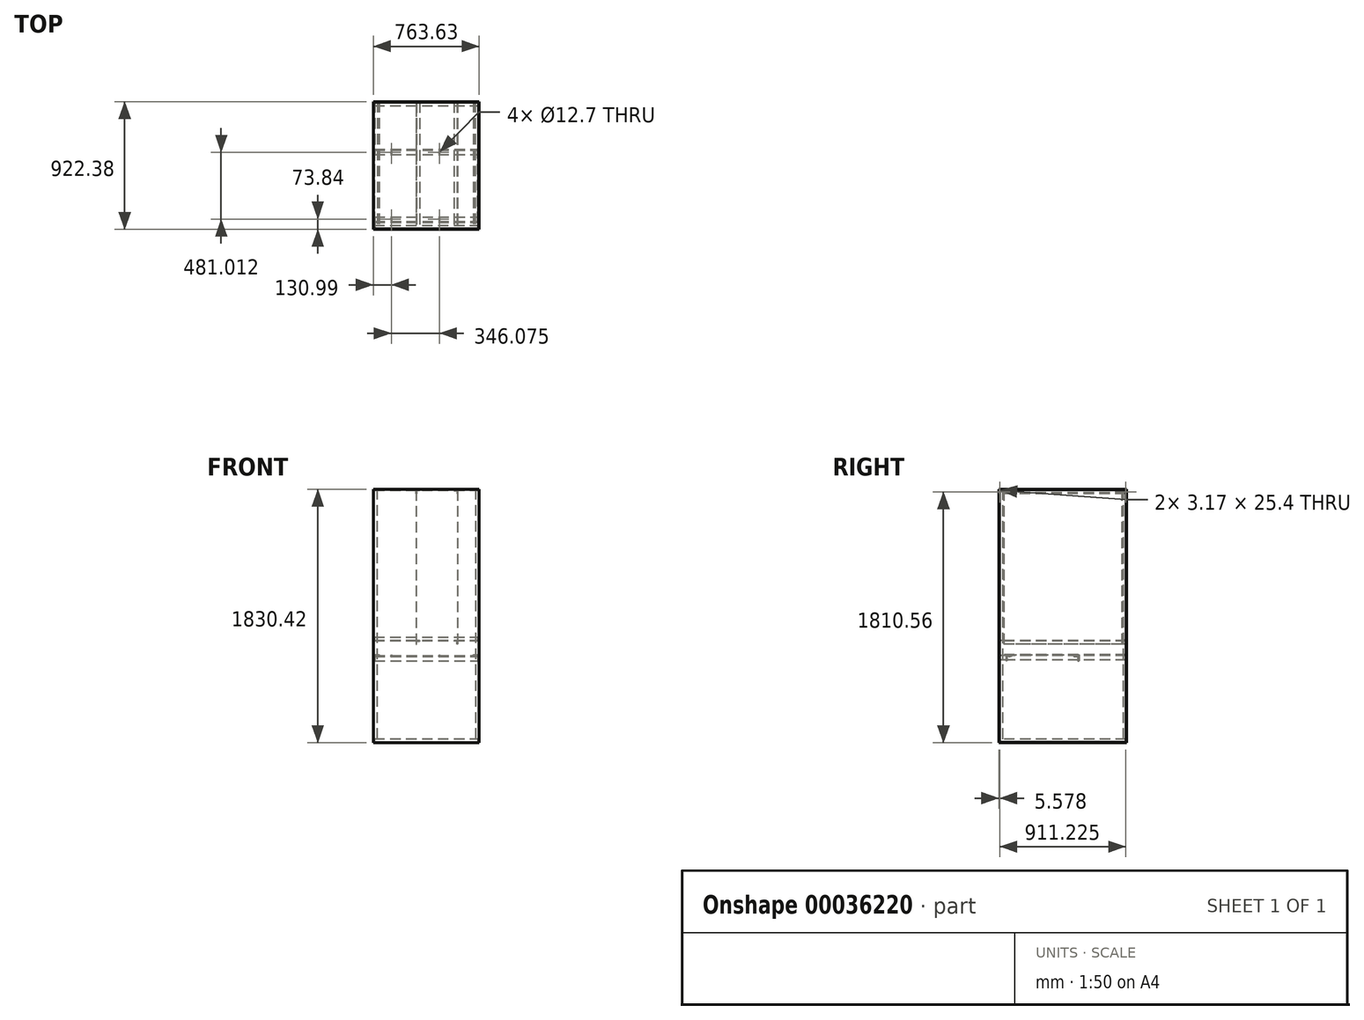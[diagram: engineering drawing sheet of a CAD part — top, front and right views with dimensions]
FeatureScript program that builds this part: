
annotation { "Feature Type Name" : "Feature", "Feature Type Description" : "" }
export const myFeature = defineFeature(function(context is Context, id is Id, definition is map)
    precondition{}
    {
        {
            var Q0;
            Q0=qCreatedBy(makeId("Front.planeOp"),FACE);
            var sketch = newSketch(context, id + "F0", { "sketchPlane" : qUnion([Q0])});
            skLineSegment(sketch, "E0", {"start": v(0, 0) * mm, "end": v(0, 25.4) * mm});
            skLineSegment(sketch, "E1", {"start": v(0, 25.4) * mm, "end": v(3.18, 25.4) * mm});
            skLineSegment(sketch, "E2", {"start": v(3.18, 25.4) * mm, "end": v(3.18, 3.17) * mm});
            skLineSegment(sketch, "E3", {"start": v(3.18, 3.17) * mm, "end": v(25.4, 3.17) * mm});
            skLineSegment(sketch, "E4", {"start": v(25.4, 3.17) * mm, "end": v(25.4, 0) * mm});
            skLineSegment(sketch, "E5", {"start": v(25.4, 0) * mm, "end": v(0, 0) * mm});
            skLineSegment(sketch, "E6", {"start": v(730.25, 0) * mm, "end": v(755.65, 0) * mm});
            skLineSegment(sketch, "E7", {"start": v(755.65, 0) * mm, "end": v(755.65, 25.4) * mm});
            skLineSegment(sketch, "E8", {"start": v(755.65, 25.4) * mm, "end": v(752.48, 25.4) * mm});
            skLineSegment(sketch, "E9", {"start": v(752.47, 25.4) * mm, "end": v(752.47, 3.18) * mm});
            skLineSegment(sketch, "E10", {"start": v(752.47, 3.18) * mm, "end": v(730.25, 3.18) * mm});
            skLineSegment(sketch, "E11", {"start": v(730.25, 3.18) * mm, "end": v(730.25, 0) * mm});
            skLineSegment(sketch, "E12", {"start": v(730.25, 1828.8) * mm, "end": v(755.65, 1828.8) * mm});
            skLineSegment(sketch, "E13", {"start": v(755.65, 1828.8) * mm, "end": v(755.65, 1803.4) * mm});
            skLineSegment(sketch, "E14", {"start": v(755.65, 1803.4) * mm, "end": v(752.48, 1803.4) * mm});
            skLineSegment(sketch, "E15", {"start": v(752.48, 1803.4) * mm, "end": v(752.48, 1825.62) * mm});
            skLineSegment(sketch, "E16", {"start": v(752.47, 1825.62) * mm, "end": v(730.25, 1825.62) * mm});
            skLineSegment(sketch, "E17", {"start": v(730.25, 1825.62) * mm, "end": v(730.25, 1828.8) * mm});
            skLineSegment(sketch, "E18", {"start": v(0, 1803.4) * mm, "end": v(0, 1828.8) * mm});
            skLineSegment(sketch, "E19", {"start": v(0, 1828.8) * mm, "end": v(25.4, 1828.8) * mm});
            skLineSegment(sketch, "E20", {"start": v(25.4, 1828.8) * mm, "end": v(25.4, 1825.62) * mm});
            skLineSegment(sketch, "E21", {"start": v(25.4, 1825.62) * mm, "end": v(3.17, 1825.62) * mm});
            skLineSegment(sketch, "E22", {"start": v(3.17, 1825.62) * mm, "end": v(3.17, 1803.4) * mm});
            skLineSegment(sketch, "E23", {"start": v(3.17, 1803.4) * mm, "end": v(0, 1803.4) * mm});
            skLineSegment(sketch, "E24", {"start": v(717.55, 635) * mm, "end": v(755.65, 635) * mm});
            skLineSegment(sketch, "E25", {"start": v(755.65, 635) * mm, "end": v(755.65, 596.9) * mm});
            skLineSegment(sketch, "E26", {"start": v(755.65, 596.9) * mm, "end": v(749.3, 596.9) * mm});
            skLineSegment(sketch, "E27", {"start": v(749.3, 596.9) * mm, "end": v(749.3, 628.65) * mm});
            skLineSegment(sketch, "E28", {"start": v(749.3, 628.65) * mm, "end": v(717.55, 628.65) * mm});
            skLineSegment(sketch, "E29", {"start": v(717.55, 628.65) * mm, "end": v(717.55, 635) * mm});
            skLineSegment(sketch, "E30", {"start": v(0, 596.9) * mm, "end": v(0, 635) * mm});
            skLineSegment(sketch, "E31", {"start": v(0, 635) * mm, "end": v(38.1, 635) * mm});
            skLineSegment(sketch, "E32", {"start": v(38.1, 635) * mm, "end": v(38.1, 628.65) * mm});
            skLineSegment(sketch, "E33", {"start": v(38.1, 628.65) * mm, "end": v(6.35, 628.65) * mm});
            skLineSegment(sketch, "E34", {"start": v(6.35, 628.65) * mm, "end": v(6.35, 596.9) * mm});
            skLineSegment(sketch, "E35", {"start": v(6.35, 596.9) * mm, "end": v(0, 596.9) * mm});
            skLineSegment(sketch, "E36", {"start": v(577.85, 736.6) * mm, "end": v(603.25, 736.6) * mm});
            skLineSegment(sketch, "E37", {"start": v(603.25, 736.6) * mm, "end": v(603.25, 711.2) * mm});
            skLineSegment(sketch, "E38", {"start": v(603.25, 711.2) * mm, "end": v(600.07, 711.2) * mm});
            skLineSegment(sketch, "E39", {"start": v(600.07, 711.2) * mm, "end": v(600.07, 733.43) * mm});
            skLineSegment(sketch, "E40", {"start": v(600.07, 733.43) * mm, "end": v(577.85, 733.43) * mm});
            skLineSegment(sketch, "E41", {"start": v(577.85, 1822.45) * mm, "end": v(603.25, 1822.45) * mm});
            skLineSegment(sketch, "E42", {"start": v(603.25, 1822.45) * mm, "end": v(603.25, 1797.05) * mm});
            skLineSegment(sketch, "E43", {"start": v(603.25, 1797.05) * mm, "end": v(600.07, 1797.05) * mm});
            skLineSegment(sketch, "E44", {"start": v(600.07, 1797.05) * mm, "end": v(600.07, 1819.27) * mm});
            skLineSegment(sketch, "E45", {"start": v(600.07, 1819.27) * mm, "end": v(577.85, 1819.27) * mm});
            skLineSegment(sketch, "E46", {"start": v(577.85, 1819.27) * mm, "end": v(577.85, 1822.45) * mm});
            skLineSegment(sketch, "E47", {"start": v(577.85, 736.6) * mm, "end": v(577.85, 733.43) * mm});
            skLineSegment(sketch, "E48", {"start": v(600.07, 733.43) * mm, "end": v(600.07, 736.6) * mm, "construction": true});
            skLineSegment(sketch, "E49", {"start": v(600.07, 1819.27) * mm, "end": v(600.07, 1822.45) * mm, "construction": true});
            skLineSegment(sketch, "E50.MirrorCS", {"start": v(307.97, 733.43) * mm, "end": v(307.97, 736.6) * mm, "construction": true});
            skLineSegment(sketch, "E51.MirrorCS", {"start": v(330.2, 736.6) * mm, "end": v(330.2, 733.43) * mm});
            skLineSegment(sketch, "E52.MirrorCS", {"start": v(330.2, 736.6) * mm, "end": v(304.8, 736.6) * mm});
            skLineSegment(sketch, "E53.MirrorCS", {"start": v(307.97, 733.43) * mm, "end": v(330.2, 733.43) * mm});
            skLineSegment(sketch, "E54.MirrorCS", {"start": v(304.8, 736.6) * mm, "end": v(304.8, 711.2) * mm});
            skLineSegment(sketch, "E55.MirrorCS", {"start": v(307.97, 711.2) * mm, "end": v(307.97, 733.43) * mm});
            skLineSegment(sketch, "E56.MirrorCS", {"start": v(304.8, 711.2) * mm, "end": v(307.97, 711.2) * mm});
            skLineSegment(sketch, "E57.MirrorCS", {"start": v(307.97, 1819.27) * mm, "end": v(307.97, 1822.45) * mm, "construction": true});
            skLineSegment(sketch, "E58.MirrorCS", {"start": v(330.2, 1822.45) * mm, "end": v(304.8, 1822.45) * mm});
            skLineSegment(sketch, "E59.MirrorCS", {"start": v(307.97, 1819.27) * mm, "end": v(330.2, 1819.27) * mm});
            skLineSegment(sketch, "E60.MirrorCS", {"start": v(304.8, 1822.45) * mm, "end": v(304.8, 1797.05) * mm});
            skLineSegment(sketch, "E61.MirrorCS", {"start": v(307.97, 1797.05) * mm, "end": v(307.97, 1819.27) * mm});
            skLineSegment(sketch, "E62.MirrorCS", {"start": v(330.2, 1819.27) * mm, "end": v(330.2, 1822.45) * mm});
            skLineSegment(sketch, "E63.MirrorCS", {"start": v(304.8, 1797.05) * mm, "end": v(307.97, 1797.05) * mm});
            skSolve(sketch);
        }
        {
            var Q0;
            Q0=qSketchRegion(id+"F0",true);
            extrude(context, id + "F1", {"entities" : qUnion([Q0]), "oppositeDirection" : true, "depth" : 914.4 * mm});
        }
        {
            var Q0;
            Q0=qCreatedBy(makeId("Top.planeOp"),FACE);
            var sketch = newSketch(context, id + "F2", { "sketchPlane" : qUnion([Q0])});
            skLineSegment(sketch, "E64", {"start": v(-3.18, 22.23) * mm, "end": v(-3.18, -3.18) * mm});
            skLineSegment(sketch, "E65", {"start": v(-3.18, -3.18) * mm, "end": v(22.23, -3.18) * mm});
            skLineSegment(sketch, "E66", {"start": v(22.23, -3.18) * mm, "end": v(22.23, 0) * mm});
            skLineSegment(sketch, "E67", {"start": v(22.23, 0) * mm, "end": v(0, 0) * mm});
            skLineSegment(sketch, "E68", {"start": v(0, 0) * mm, "end": v(0, 22.23) * mm});
            skLineSegment(sketch, "E69", {"start": v(0, 22.23) * mm, "end": v(-3.18, 22.23) * mm});
            skLineSegment(sketch, "E70", {"start": v(733.42, -3.18) * mm, "end": v(758.83, -3.18) * mm});
            skLineSegment(sketch, "E71", {"start": v(758.83, -3.18) * mm, "end": v(758.83, 22.23) * mm});
            skLineSegment(sketch, "E72", {"start": v(758.83, 22.23) * mm, "end": v(755.65, 22.23) * mm});
            skLineSegment(sketch, "E73", {"start": v(755.65, 22.23) * mm, "end": v(755.65, 0) * mm});
            skLineSegment(sketch, "E74", {"start": v(755.65, 0) * mm, "end": v(733.42, 0) * mm});
            skLineSegment(sketch, "E75", {"start": v(733.42, 0) * mm, "end": v(733.42, -3.18) * mm});
            skLineSegment(sketch, "E76", {"start": v(0, 892.17) * mm, "end": v(0, 914.4) * mm});
            skLineSegment(sketch, "E77", {"start": v(0, 914.4) * mm, "end": v(22.23, 914.4) * mm});
            skLineSegment(sketch, "E78", {"start": v(22.23, 914.4) * mm, "end": v(22.23, 917.58) * mm});
            skLineSegment(sketch, "E79", {"start": v(22.23, 917.58) * mm, "end": v(-3.18, 917.58) * mm});
            skLineSegment(sketch, "E80", {"start": v(-3.18, 917.58) * mm, "end": v(-3.18, 892.17) * mm});
            skLineSegment(sketch, "E81", {"start": v(-3.18, 892.17) * mm, "end": v(0, 892.17) * mm});
            skLineSegment(sketch, "E82", {"start": v(733.42, 914.4) * mm, "end": v(755.65, 914.4) * mm});
            skLineSegment(sketch, "E83", {"start": v(755.65, 914.4) * mm, "end": v(755.65, 892.17) * mm});
            skLineSegment(sketch, "E84", {"start": v(755.65, 892.18) * mm, "end": v(758.83, 892.18) * mm});
            skLineSegment(sketch, "E85", {"start": v(758.83, 892.17) * mm, "end": v(758.83, 917.58) * mm});
            skLineSegment(sketch, "E86", {"start": v(758.83, 917.58) * mm, "end": v(733.42, 917.58) * mm});
            skLineSegment(sketch, "E87", {"start": v(733.42, 917.58) * mm, "end": v(733.42, 914.4) * mm});
            skSolve(sketch);
        }
        {
            var Q0;
            Q0=qSketchRegion(id+"F2",true);
            extrude(context, id + "F3", {"entities" : qUnion([Q0]), "depth" : 1828.8 * mm});
        }
        {
            var Q0;
            Q0=makeQuery(id+"F1.opExtrude","SWEPT_FACE",FACE,{"disambiguationData":[OSD([sQuery(id+"F0.wireOp",EDGE,"E15")])]});
            var sketch = newSketch(context, id + "F4", { "sketchPlane" : qUnion([Q0])});
            skLineSegment(sketch, "E88", {"start": v(-25.4, 3.18) * mm, "end": v(0, 3.18) * mm});
            skLineSegment(sketch, "E89", {"start": v(0, 3.18) * mm, "end": v(0, 28.58) * mm});
            skLineSegment(sketch, "E90", {"start": v(0, 28.58) * mm, "end": v(-3.17, 28.58) * mm});
            skLineSegment(sketch, "E91", {"start": v(-3.18, 28.58) * mm, "end": v(-3.17, 6.35) * mm});
            skLineSegment(sketch, "E92", {"start": v(-3.18, 6.35) * mm, "end": v(-25.4, 6.35) * mm});
            skLineSegment(sketch, "E93", {"start": v(-25.4, 6.35) * mm, "end": v(-25.4, 3.18) * mm});
            skLineSegment(sketch, "E94", {"start": v(0, 1800.22) * mm, "end": v(0, 1825.62) * mm});
            skLineSegment(sketch, "E95", {"start": v(0, 1825.62) * mm, "end": v(-25.4, 1825.62) * mm});
            skLineSegment(sketch, "E96", {"start": v(-25.4, 1825.62) * mm, "end": v(-25.4, 1822.45) * mm});
            skLineSegment(sketch, "E97", {"start": v(-25.4, 1822.45) * mm, "end": v(-3.18, 1822.45) * mm});
            skLineSegment(sketch, "E98", {"start": v(-3.18, 1822.45) * mm, "end": v(-3.18, 1800.22) * mm});
            skLineSegment(sketch, "E99", {"start": v(-3.18, 1800.22) * mm, "end": v(0, 1800.22) * mm});
            skLineSegment(sketch, "E100", {"start": v(-914.4, 1800.22) * mm, "end": v(-914.4, 1825.62) * mm});
            skLineSegment(sketch, "E101", {"start": v(-914.4, 1825.62) * mm, "end": v(-889, 1825.62) * mm});
            skLineSegment(sketch, "E102", {"start": v(-889, 1825.62) * mm, "end": v(-889, 1822.45) * mm});
            skLineSegment(sketch, "E103", {"start": v(-889, 1822.45) * mm, "end": v(-911.22, 1822.45) * mm});
            skLineSegment(sketch, "E104", {"start": v(-911.23, 1822.45) * mm, "end": v(-911.23, 1800.22) * mm});
            skLineSegment(sketch, "E105", {"start": v(-911.22, 1800.22) * mm, "end": v(-914.4, 1800.22) * mm});
            skLineSegment(sketch, "E106", {"start": v(-914.4, 28.58) * mm, "end": v(-914.4, 3.18) * mm});
            skLineSegment(sketch, "E107", {"start": v(-914.4, 3.18) * mm, "end": v(-889, 3.18) * mm});
            skLineSegment(sketch, "E108", {"start": v(-889, 3.18) * mm, "end": v(-889, 6.35) * mm});
            skLineSegment(sketch, "E109", {"start": v(-889, 6.35) * mm, "end": v(-911.22, 6.35) * mm});
            skLineSegment(sketch, "E110", {"start": v(-911.22, 6.35) * mm, "end": v(-911.22, 28.58) * mm});
            skLineSegment(sketch, "E111", {"start": v(-911.22, 28.58) * mm, "end": v(-914.4, 28.58) * mm});
            skLineSegment(sketch, "E112", {"start": v(-573.09, 590.55) * mm, "end": v(-573.09, 628.65) * mm});
            skLineSegment(sketch, "E113", {"start": v(-573.09, 628.65) * mm, "end": v(-534.99, 628.65) * mm});
            skLineSegment(sketch, "E114", {"start": v(-534.99, 628.65) * mm, "end": v(-534.99, 622.3) * mm});
            skLineSegment(sketch, "E115", {"start": v(-534.99, 622.3) * mm, "end": v(-566.74, 622.3) * mm});
            skLineSegment(sketch, "E116", {"start": v(-566.74, 622.3) * mm, "end": v(-566.74, 590.55) * mm});
            skLineSegment(sketch, "E117", {"start": v(-566.74, 590.55) * mm, "end": v(-573.09, 590.55) * mm});
            skLineSegment(sketch, "E118", {"start": v(-550.86, 622.3) * mm, "end": v(-550.86, 628.65) * mm, "construction": true});
            skLineSegment(sketch, "E119", {"start": v(-47.63, 590.55) * mm, "end": v(-47.63, 628.65) * mm});
            skLineSegment(sketch, "E120", {"start": v(-47.63, 628.65) * mm, "end": v(-85.72, 628.65) * mm});
            skLineSegment(sketch, "E121", {"start": v(-85.73, 628.65) * mm, "end": v(-85.73, 622.3) * mm});
            skLineSegment(sketch, "E122", {"start": v(-85.72, 622.3) * mm, "end": v(-53.98, 622.3) * mm});
            skLineSegment(sketch, "E123", {"start": v(-53.98, 622.3) * mm, "end": v(-53.98, 590.55) * mm});
            skLineSegment(sketch, "E124", {"start": v(-53.97, 590.55) * mm, "end": v(-47.63, 590.55) * mm});
            skLineSegment(sketch, "E125", {"start": v(-69.85, 622.3) * mm, "end": v(-69.85, 628.65) * mm, "construction": true});
            skLineSegment(sketch, "E126", {"start": v(-550.86, 625.48) * mm, "end": v(-69.85, 625.48) * mm, "construction": true});
            skLineSegment(sketch, "E127", {"start": v(0, 736.6) * mm, "end": v(0, 762) * mm});
            skLineSegment(sketch, "E128", {"start": v(0, 762) * mm, "end": v(-3.17, 762) * mm});
            skLineSegment(sketch, "E129", {"start": v(-3.17, 762) * mm, "end": v(-3.17, 739.78) * mm});
            skLineSegment(sketch, "E130", {"start": v(-3.17, 739.78) * mm, "end": v(-25.4, 739.78) * mm});
            skLineSegment(sketch, "E131", {"start": v(-25.4, 739.78) * mm, "end": v(-25.4, 736.6) * mm});
            skLineSegment(sketch, "E132", {"start": v(-25.4, 736.6) * mm, "end": v(0, 736.6) * mm});
            skLineSegment(sketch, "E133", {"start": v(-889, 736.6) * mm, "end": v(-914.4, 736.6) * mm});
            skLineSegment(sketch, "E134", {"start": v(-914.4, 736.6) * mm, "end": v(-914.4, 762) * mm});
            skLineSegment(sketch, "E135", {"start": v(-914.4, 762) * mm, "end": v(-911.22, 762) * mm});
            skLineSegment(sketch, "E136", {"start": v(-911.23, 762) * mm, "end": v(-911.23, 739.78) * mm});
            skLineSegment(sketch, "E137", {"start": v(-911.22, 739.78) * mm, "end": v(-889, 739.78) * mm});
            skLineSegment(sketch, "E138", {"start": v(-889, 739.78) * mm, "end": v(-889, 736.6) * mm});
            skSolve(sketch);
        }
        {
            var Q0;
            Q0=qSketchRegion(id+"F4",true);
            var Q1;
            Q1=makeQuery(id+"F1.opExtrude","SWEPT_FACE",FACE,{"disambiguationData":[OSD([sQuery(id+"F0.wireOp",EDGE,"E2")])]});
            extrude(context, id + "F5", {"entities" : qUnion([Q0]), "endBound" : BoundingType.UP_TO_SURFACE, "endBoundEntityFace" : qUnion([Q1]), "depth" : 25.4 * mm});
        }
        {
            var Q0;
            Q0=makeQuery(id+"F5.opExtrude","SWEPT_FACE",FACE,{"disambiguationData":[OSD([sQuery(id+"F4.wireOp",EDGE,"E115")])]});
            var sketch = newSketch(context, id + "F6", { "sketchPlane" : qUnion([Q0])});
            skLineSegment(sketch, "E139.bottom", {"start": v(127, -69.85) * mm, "end": v(473.07, -69.85) * mm, "construction": true});
            skLineSegment(sketch, "E139.top", {"start": v(127, -550.86) * mm, "end": v(473.07, -550.86) * mm, "construction": true});
            skLineSegment(sketch, "E139.left", {"start": v(473.07, -69.85) * mm, "end": v(473.07, -550.86) * mm, "construction": true});
            skLineSegment(sketch, "E139.right", {"start": v(127, -69.85) * mm, "end": v(127, -550.86) * mm, "construction": true});
            skLineSegment(sketch, "E140", {"start": v(473.07, -550.86) * mm, "end": v(3.17, -550.86) * mm, "construction": true});
            skLineSegment(sketch, "E141", {"start": v(127, -550.86) * mm, "end": v(752.47, -550.86) * mm, "construction": true});
            skCircle(sketch, "E142", {"center": v(127, -69.85) * mm, "radius": 6.35 * mm});
            skCircle(sketch, "E143", {"center": v(473.07, -69.85) * mm, "radius": 6.35 * mm});
            skCircle(sketch, "E144", {"center": v(473.07, -550.86) * mm, "radius": 6.35 * mm});
            skCircle(sketch, "E145", {"center": v(127, -550.86) * mm, "radius": 6.35 * mm});
            skLineSegment(sketch, "E146.bottom", {"start": v(3.17, -47.62) * mm, "end": v(6.35, -47.62) * mm});
            skLineSegment(sketch, "E146.top", {"start": v(3.17, -573.09) * mm, "end": v(6.35, -573.09) * mm});
            skLineSegment(sketch, "E146.left", {"start": v(3.17, -47.62) * mm, "end": v(3.17, -573.09) * mm});
            skLineSegment(sketch, "E146.right", {"start": v(6.35, -47.62) * mm, "end": v(6.35, -573.09) * mm});
            skLineSegment(sketch, "E147.bottom", {"start": v(749.3, -47.62) * mm, "end": v(752.47, -47.62) * mm});
            skLineSegment(sketch, "E147.top", {"start": v(749.3, -573.09) * mm, "end": v(752.47, -573.09) * mm});
            skLineSegment(sketch, "E147.left", {"start": v(749.3, -47.62) * mm, "end": v(749.3, -573.09) * mm});
            skLineSegment(sketch, "E147.right", {"start": v(752.47, -47.62) * mm, "end": v(752.47, -573.09) * mm});
            skSolve(sketch);
        }
        {
            var Q0;
            Q0=makeQuery(id+"F6.imprint","IMPRINT",FACE,{"disambiguationData":[TD([[makeQuery(id+"F6.imprint","IMPRINT",EDGE,{"derivedFrom":sQuery(id+"F6.wireOp",EDGE,"E143")}),1.0]])]});
            var Q1;
            Q1=makeQuery(id+"F6.imprint","IMPRINT",FACE,{"disambiguationData":[TD([[makeQuery(id+"F6.imprint","IMPRINT",EDGE,{"derivedFrom":sQuery(id+"F6.wireOp",EDGE,"E144")}),1.0]])]});
            var Q2;
            Q2=makeQuery(id+"F6.imprint","IMPRINT",FACE,{"disambiguationData":[TD([[makeQuery(id+"F6.imprint","IMPRINT",EDGE,{"derivedFrom":sQuery(id+"F6.wireOp",EDGE,"E145")}),1.0]])]});
            var Q3;
            Q3=makeQuery(id+"F6.imprint","IMPRINT",FACE,{"disambiguationData":[TD([[makeQuery(id+"F6.imprint","IMPRINT",EDGE,{"derivedFrom":sQuery(id+"F6.wireOp",EDGE,"E142")}),1.0]])]});
            var Q4;
            {var subQ5=sQuery(id+"F6.wireOp",EDGE,"E146.bottom");Q4=makeQuery(id+"F6.imprint","IMPRINT",FACE,{"disambiguationData":[TD([[makeQuery(id+"F6.imprint","IMPRINT",EDGE,{"derivedFrom":subQ5}),-1.0]])]});}
            var Q5;
            {var subQ5=sQuery(id+"F6.wireOp",EDGE,"E147.bottom");Q5=makeQuery(id+"F6.imprint","IMPRINT",FACE,{"disambiguationData":[TD([[makeQuery(id+"F6.imprint","IMPRINT",EDGE,{"derivedFrom":subQ5}),-1.0]])]});}
            var Q6;
            {var subQ5=sQuery(id+"F6.wireOp",EDGE,"E146.top");Q6=makeQuery(id+"F6.imprint","IMPRINT",FACE,{"disambiguationData":[TD([[makeQuery(id+"F6.imprint","IMPRINT",EDGE,{"derivedFrom":subQ5}),1.0]])]});}
            var Q7;
            {var subQ0=sQuery(id+"F4.wireOp",EDGE,"E115");var subQ4=sQuery(id+"F6.wireOp",EDGE,"E146.left");var subQ6=makeQuery(id+"F5.opExtrude","SWEPT_EDGE",EDGE,{"disambiguationData":[OSD([sQuery(id+"F4.wireOp",EDGE,"E114"),subQ0])]});var subQ8=makeQuery(id+"F6.imprint","INTERSECT",VERTEX,{"derivedFrom":[subQ6,subQ4]});Q7=makeQuery(id+"F6.imprint","IMPRINT",FACE,{"disambiguationData":[TD([[makeQuery(id+"F6.imprint","IMPRINT",EDGE,{"disambiguationData":[TD([[subQ8,-1.0]])],"derivedFrom":subQ4}),1.0]])]});}
            var Q8;
            {var subQ0=sQuery(id+"F4.wireOp",EDGE,"E115");var subQ2=sQuery(id+"F6.wireOp",EDGE,"E147.left");var subQ6=makeQuery(id+"F5.opExtrude","SWEPT_EDGE",EDGE,{"disambiguationData":[OSD([sQuery(id+"F4.wireOp",EDGE,"E114"),subQ0])]});var subQ7=makeQuery(id+"F6.imprint","INTERSECT",VERTEX,{"derivedFrom":[subQ6,subQ2]});Q8=makeQuery(id+"F6.imprint","IMPRINT",FACE,{"disambiguationData":[TD([[makeQuery(id+"F6.imprint","IMPRINT",EDGE,{"disambiguationData":[TD([[subQ7,-1.0]])],"derivedFrom":subQ2}),1.0]])]});}
            var Q9;
            {var subQ5=sQuery(id+"F6.wireOp",EDGE,"E147.top");Q9=makeQuery(id+"F6.imprint","IMPRINT",FACE,{"disambiguationData":[TD([[makeQuery(id+"F6.imprint","IMPRINT",EDGE,{"derivedFrom":subQ5}),1.0]])]});}
            var Q10;
            Q10=makeQuery(id+"F5.opExtrude","SWEPT_FACE",FACE,{"disambiguationData":[OSD([sQuery(id+"F4.wireOp",EDGE,"E117")])]});
            extrude(context, id + "F7", {"entities" : qUnion([Q0, Q1, Q2, Q3, Q4, Q5, Q6, Q7, Q8, Q9]), "operationType" : NewBodyOperationType.REMOVE, "oppositeDirection" : true, "endBoundEntityFace" : qUnion([Q10]), "depth" : 50.8 * mm, "hasSecondDirection" : true, "secondDirectionOppositeDirection" : false, "secondDirectionDepth" : 50.8 * mm});
        }
        {
            var Q0;
            Q0=makeQuery(id+"F1.opExtrude","SWEPT_FACE",FACE,{"disambiguationData":[OSD([sQuery(id+"F0.wireOp",EDGE,"E37")])]});
            var sketch = newSketch(context, id + "F8", { "sketchPlane" : qUnion([Q0])});
            skLineSegment(sketch, "E148.bottom", {"start": v(31.75, 1822.45) * mm, "end": v(882.65, 1822.45) * mm});
            skLineSegment(sketch, "E148.top", {"start": v(31.75, 711.2) * mm, "end": v(882.65, 711.2) * mm});
            skLineSegment(sketch, "E148.left", {"start": v(31.75, 1822.45) * mm, "end": v(31.75, 711.2) * mm});
            skLineSegment(sketch, "E148.right", {"start": v(882.65, 1822.45) * mm, "end": v(882.65, 711.2) * mm});
            skSolve(sketch);
        }
        {
            var Q0;
            Q0=qSketchRegion(id+"F8",true);
            extrude(context, id + "F9", {"entities" : qUnion([Q0]), "depth" : 1.02 * mm});
        }
        {
            var Q0;
            Q0=makeQuery(id+"F1.opExtrude","SWEPT_FACE",FACE,{"disambiguationData":[OSD([sQuery(id+"F0.wireOp",EDGE,"E46")])]});
            var sketch = newSketch(context, id + "F10", { "sketchPlane" : qUnion([Q0])});
            skLineSegment(sketch, "E149.bottom", {"start": v(-3.18, 1822.45) * mm, "end": v(0, 1822.45) * mm});
            skLineSegment(sketch, "E149.top", {"start": v(-3.18, 1797.05) * mm, "end": v(0, 1797.05) * mm});
            skLineSegment(sketch, "E149.left", {"start": v(-3.18, 1822.45) * mm, "end": v(-3.18, 1797.05) * mm});
            skLineSegment(sketch, "E149.right", {"start": v(0, 1822.45) * mm, "end": v(0, 1797.05) * mm});
            skLineSegment(sketch, "E150.bottom", {"start": v(-914.4, 1822.45) * mm, "end": v(-911.22, 1822.45) * mm});
            skLineSegment(sketch, "E150.top", {"start": v(-914.4, 1797.05) * mm, "end": v(-911.22, 1797.05) * mm});
            skLineSegment(sketch, "E150.left", {"start": v(-914.4, 1822.45) * mm, "end": v(-914.4, 1797.05) * mm});
            skLineSegment(sketch, "E150.right", {"start": v(-911.22, 1822.45) * mm, "end": v(-911.22, 1797.05) * mm});
            skSolve(sketch);
        }
        {
            var Q0;
            Q0=qSketchRegion(id+"F10",true);
            var Q1;
            Q1=makeQuery(id+"F1.opExtrude","SWEPT_FACE",FACE,{"disambiguationData":[OSD([sQuery(id+"F0.wireOp",EDGE,"E60.MirrorCS")])]});
            extrude(context, id + "F11", {"entities" : qUnion([Q0]), "operationType" : NewBodyOperationType.REMOVE, "endBound" : BoundingType.THROUGH_ALL, "depth" : 25.4 * mm, "hasSecondDirection" : true, "secondDirectionBound" : BoundingType.THROUGH_ALL, "secondDirectionOppositeDirection" : true, "secondDirectionBoundEntityFace" : qUnion([Q1]), "secondDirectionDepth" : 508 * mm});
        }
        {
            var Q0;
            Q0=makeQuery(id+"F3.opExtrude","SWEPT_FACE",FACE,{"disambiguationData":[OSD([sQuery(id+"F2.wireOp",EDGE,"E71")])]});
            var sketch = newSketch(context, id + "F12", { "sketchPlane" : qUnion([Q0])});
            skLineSegment(sketch, "E151.bottom", {"start": v(0, 1826.02) * mm, "end": v(914.4, 1826.02) * mm});
            skLineSegment(sketch, "E151.top", {"start": v(0, 2.78) * mm, "end": v(914.4, 2.78) * mm});
            skLineSegment(sketch, "E151.left", {"start": v(0, 1826.02) * mm, "end": v(0, 2.78) * mm});
            skLineSegment(sketch, "E151.right", {"start": v(914.4, 1826.02) * mm, "end": v(914.4, 2.78) * mm});
            skLineSegment(sketch, "E152", {"start": v(914.4, 2.78) * mm, "end": v(917.58, 0) * mm, "construction": true});
            skLineSegment(sketch, "E153", {"start": v(-3.18, 0) * mm, "end": v(0, 2.78) * mm, "construction": true});
            skLineSegment(sketch, "E154", {"start": v(-3.17, 1828.8) * mm, "end": v(0, 1826.02) * mm, "construction": true});
            skLineSegment(sketch, "E155", {"start": v(914.4, 1826.02) * mm, "end": v(917.58, 1828.8) * mm, "construction": true});
            skSolve(sketch);
        }
        {
            var Q0;
            Q0=makeQuery(id+"F1.opExtrude","SWEPT_FACE",FACE,{"disambiguationData":[OSD([sQuery(id+"F0.wireOp",EDGE,"E60.MirrorCS")])]});
            var sketch = newSketch(context, id + "F13", { "sketchPlane" : qUnion([Q0])});
            skLineSegment(sketch, "E156.bottom", {"start": v(-882.65, 1822.45) * mm, "end": v(-31.75, 1822.45) * mm});
            skLineSegment(sketch, "E156.top", {"start": v(-882.65, 711.2) * mm, "end": v(-31.75, 711.2) * mm});
            skLineSegment(sketch, "E156.left", {"start": v(-882.65, 1822.45) * mm, "end": v(-882.65, 711.2) * mm});
            skLineSegment(sketch, "E156.right", {"start": v(-31.75, 1822.45) * mm, "end": v(-31.75, 711.2) * mm});
            skSolve(sketch);
        }
        {
            var Q0;
            Q0=qSketchRegion(id+"F13",true);
            extrude(context, id + "F14", {"entities" : qUnion([Q0]), "depth" : 1.02 * mm});
        }
        {
            var Q0;
            Q0=makeQuery(id+"F3.opExtrude","SWEPT_FACE",FACE,{"disambiguationData":[OSD([sQuery(id+"F2.wireOp",EDGE,"E80")])]});
            var sketch = newSketch(context, id + "F15", { "sketchPlane" : qUnion([Q0])});
            skLineSegment(sketch, "E157.bottom", {"start": v(-917.58, 1828.8) * mm, "end": v(3.17, 1828.8) * mm});
            skLineSegment(sketch, "E157.top", {"start": v(-917.58, 0) * mm, "end": v(3.18, 0) * mm});
            skLineSegment(sketch, "E157.left", {"start": v(-917.58, 1828.8) * mm, "end": v(-917.58, 0) * mm});
            skLineSegment(sketch, "E157.right", {"start": v(3.17, 1828.8) * mm, "end": v(3.18, 0) * mm});
            skSolve(sketch);
        }
        {
            var Q0;
            Q0=qSketchRegion(id+"F12",true);
            extrude(context, id + "F16", {"entities" : qUnion([Q0]), "depth" : 0.81 * mm});
        }
        {
            var Q0;
            Q0=qSketchRegion(id+"F15",true);
            extrude(context, id + "F17", {"entities" : qUnion([Q0]), "depth" : 0.81 * mm});
        }
        {
            var Q0;
            Q0=makeQuery(id+"F1.opExtrude","SWEPT_FACE",FACE,{"disambiguationData":[OSD([sQuery(id+"F0.wireOp",EDGE,"E19")])]});
            var sketch = newSketch(context, id + "F18", { "sketchPlane" : qUnion([Q0])});
            skLineSegment(sketch, "E158.bottom", {"start": v(755.65, 914.4) * mm, "end": v(-3.18, 914.4) * mm});
            skLineSegment(sketch, "E158.top", {"start": v(755.65, 0) * mm, "end": v(-3.18, 0) * mm});
            skLineSegment(sketch, "E158.left", {"start": v(755.65, 914.4) * mm, "end": v(755.65, 0) * mm});
            skLineSegment(sketch, "E158.right", {"start": v(-3.18, 914.4) * mm, "end": v(-3.17, 0) * mm});
            skSolve(sketch);
        }
        {
            var Q0;
            Q0=qSketchRegion(id+"F18",true);
            extrude(context, id + "F19", {"entities" : qUnion([Q0]), "depth" : 0.81 * mm});
        }
        {
            var Q0;
            Q0=makeQuery(id+"F1.opExtrude","SWEPT_FACE",FACE,{"disambiguationData":[OSD([sQuery(id+"F0.wireOp",EDGE,"E6")])]});
            var sketch = newSketch(context, id + "F20", { "sketchPlane" : qUnion([Q0])});
            skLineSegment(sketch, "E159.bottom", {"start": v(755.65, 0) * mm, "end": v(0, 0) * mm});
            skLineSegment(sketch, "E159.top", {"start": v(755.65, -914.4) * mm, "end": v(0, -914.4) * mm});
            skLineSegment(sketch, "E159.left", {"start": v(755.65, 0) * mm, "end": v(755.65, -914.4) * mm});
            skLineSegment(sketch, "E159.right", {"start": v(0, 0) * mm, "end": v(0, -914.4) * mm});
            skSolve(sketch);
        }
        {
            var Q0;
            Q0=qSketchRegion(id+"F20",true);
            extrude(context, id + "F21", {"entities" : qUnion([Q0]), "depth" : 0.81 * mm});
        }
        {
            var Q0;
            Q0=makeQuery(id+"F3.opExtrude","SWEPT_FACE",FACE,{"disambiguationData":[OSD([sQuery(id+"F2.wireOp",EDGE,"E86")])]});
            var sketch = newSketch(context, id + "F22", { "sketchPlane" : qUnion([Q0])});
            skLineSegment(sketch, "E160.bottom", {"start": v(-755.65, 1828.8) * mm, "end": v(0, 1828.8) * mm});
            skLineSegment(sketch, "E160.top", {"start": v(-755.65, 0) * mm, "end": v(0, 0) * mm});
            skLineSegment(sketch, "E160.left", {"start": v(-755.65, 1828.8) * mm, "end": v(-755.65, 0) * mm});
            skLineSegment(sketch, "E160.right", {"start": v(0, 1828.8) * mm, "end": v(0, 0) * mm});
            skSolve(sketch);
        }
        {
            var Q0;
            Q0=qSketchRegion(id+"F22",true);
            extrude(context, id + "F23", {"entities" : qUnion([Q0]), "depth" : 0.81 * mm});
        }
        {
            var Q0;
            Q0=makeQuery(id+"F3.opExtrude","SWEPT_FACE",FACE,{"disambiguationData":[OSD([sQuery(id+"F2.wireOp",EDGE,"E65")])]});
            var sketch = newSketch(context, id + "F24", { "sketchPlane" : qUnion([Q0])});
            skLineSegment(sketch, "E161.bottom", {"start": v(-3.18, 1828.8) * mm, "end": v(758.83, 1828.8) * mm});
            skLineSegment(sketch, "E161.top", {"start": v(-3.18, 0) * mm, "end": v(758.83, 0) * mm});
            skLineSegment(sketch, "E161.left", {"start": v(-3.18, 1828.8) * mm, "end": v(-3.18, 0) * mm});
            skLineSegment(sketch, "E161.right", {"start": v(758.83, 1828.8) * mm, "end": v(758.83, 0) * mm});
            skSolve(sketch);
        }
        {
            var Q0;
            Q0=qSketchRegion(id+"F24",true);
            extrude(context, id + "F25", {"entities" : qUnion([Q0]), "depth" : 0.81 * mm});
        }
    });
